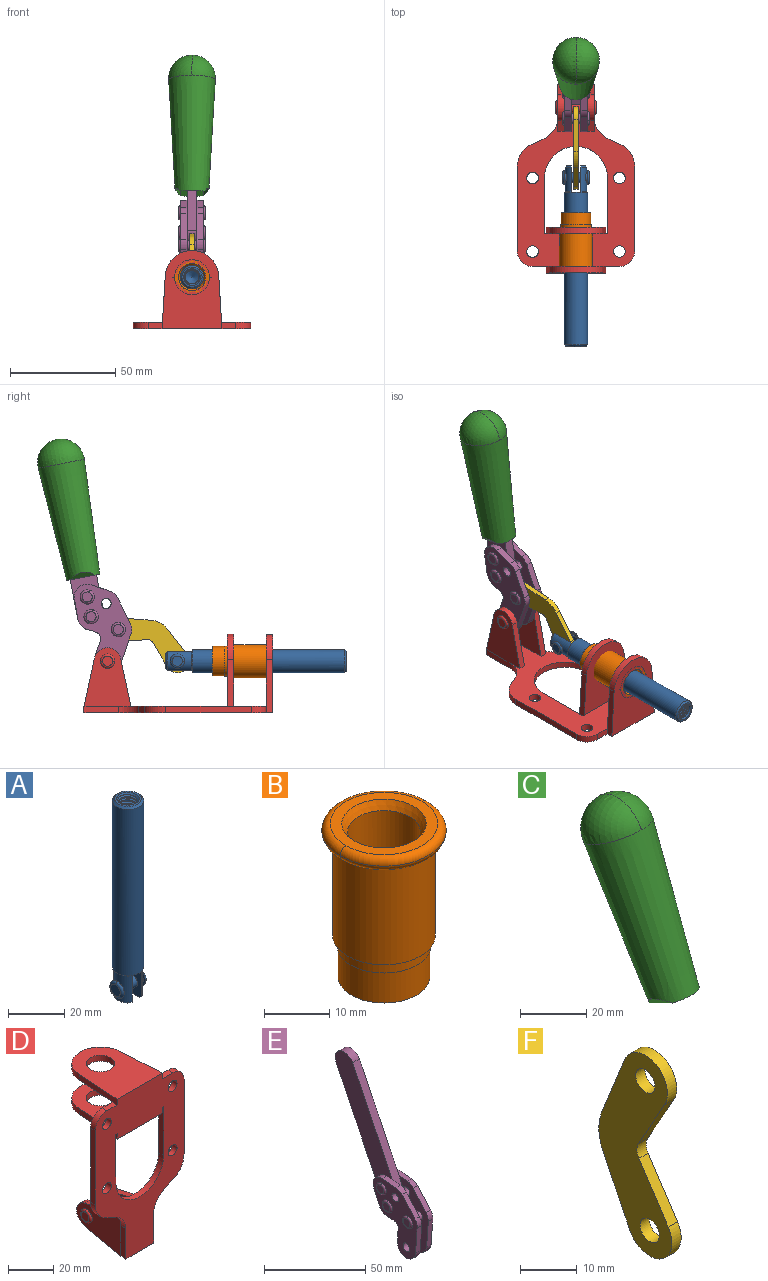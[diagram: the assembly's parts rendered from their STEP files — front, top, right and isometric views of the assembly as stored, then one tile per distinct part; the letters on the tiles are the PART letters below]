
ASSEMBLY  parts=6 mates=6
PART A: 48 faces, bbox 12.6x11.1x86.1 mm
  f0: torus R=2.41mm, axis (-1,0,0), area 15mm2, adj f30,f32,f34
  f1: torus R=2.41mm, axis (-1,0,0), area 15mm2, adj f29,f31,f33
  f2: cylinder r=5.54mm len=72.39mm, axis (0,0,1), area 2518.5mm2, adj f3,f4,f42,f43
  f3: cone r=5.54mm half-angle=45deg, axis (0,0,1), area 7.6mm2, adj f2,f5,f41
  f4: cone r=5.54mm half-angle=45deg, axis (0,0,-1), area 34.9mm2, adj f2,f39
  f5: cylinder r=5.08mm len=11.48mm, axis (0,0,1), area 108.3mm2, adj f3,f7,f8,f41
  f6: cylinder r=2.41mm len=4.83mm, axis (-1,0,0), area 71.2mm2, adj f40,f41
  f7: cylinder r=2.41mm len=4.83mm, axis (-1,0,0), area 7.6mm2, adj f5,f34
  f8: cone r=5.08mm half-angle=45deg, axis (0,0,1), area 10.6mm2, adj f5,f37,f41
  f9: cone r=3.98mm half-angle=45deg, axis (0,0,1), area 17.6mm2, adj f27,f39,f45,f46,f47
  f10: cylinder r=2.41mm len=4.83mm, axis (-1,0,0), area 7.6mm2, adj f33,f38
  f11: cylinder r=3.2mm len=6.4mm, axis (0,0,1), area 78.4mm2, adj f12,f28,f44,f45,f47
  f12: cylinder r=3.2mm len=6.4mm, axis (0,0,1), area 10.5mm2, adj f11,f13,f45,f47
  f13: cylinder r=3.2mm len=6.4mm, axis (0,0,1), area 10.5mm2, adj f12,f14,f45,f47
  f14: cylinder r=3.2mm len=6.4mm, axis (0,0,1), area 10.5mm2, adj f13,f15,f45,f47
  f15: cylinder r=3.2mm len=6.4mm, axis (0,0,1), area 10.5mm2, adj f14,f16,f45,f47
  f16: cylinder r=3.2mm len=6.4mm, axis (0,0,1), area 10.5mm2, adj f15,f17,f45,f47
  f17: cylinder r=3.2mm len=6.4mm, axis (0,0,1), area 10.5mm2, adj f16,f18,f45,f47
  f18: cylinder r=3.2mm len=6.4mm, axis (0,0,1), area 10.5mm2, adj f17,f19,f45,f47
  f19: cylinder r=3.2mm len=6.4mm, axis (0,0,1), area 10.5mm2, adj f18,f20,f45,f47
  f20: cylinder r=3.2mm len=6.4mm, axis (0,0,1), area 10.5mm2, adj f19,f21,f45,f47
  f21: cylinder r=3.2mm len=6.4mm, axis (0,0,1), area 10.5mm2, adj f20,f22,f45,f47
  f22: cylinder r=3.2mm len=6.4mm, axis (0,0,1), area 10.5mm2, adj f21,f23,f45,f47
  f23: cylinder r=3.2mm len=6.4mm, axis (0,0,1), area 10.5mm2, adj f22,f24,f45,f47
  f24: cylinder r=3.2mm len=6.4mm, axis (0,0,1), area 10.5mm2, adj f23,f25,f45,f47
  f25: cylinder r=3.2mm len=6.4mm, axis (0,0,1), area 10.5mm2, adj f24,f26,f45,f47
  f26: cylinder r=3.2mm len=6.4mm, axis (0,0,1), area 10.5mm2, adj f25,f27,f45,f47
  f27: cylinder r=3.2mm len=6.4mm, axis (0,0,1), area 7.4mm2, adj f9,f26,f45,f47
  f28: cone r=3.2mm half-angle=60deg, axis (0,0,1), area 37.2mm2, adj f11
  f29: plane 4.83x4.83mm, normal (-1,0,0), area 18.3mm2, adj f1,f31
  f30: plane 4.83x4.83mm, normal (1,0,0), area 18.3mm2, adj f0,f32
  f31: torus R=2.41mm, axis (-1,0,0), area 15mm2, adj f1,f29,f33
  f32: torus R=2.41mm, axis (-1,0,0), area 15mm2, adj f0,f30,f34
  f33: plane 6.83x6.83mm, normal (1,0,0), area 18.3mm2, adj f1,f10,f31
  f34: plane 6.83x6.83mm, normal (-1,0,0), area 18.3mm2, adj f0,f7,f32
  f35: cone r=5.08mm half-angle=45deg, axis (0,0,1), area 10.6mm2, adj f36,f38,f40
  f36: plane 7.25x1.97mm, normal (0,0,-1), area 10mm2, adj f35,f40
  f37: plane 7.25x1.97mm, normal (0,0,-1), area 10mm2, adj f8,f41
  f38: cylinder r=5.08mm len=11.48mm, axis (0,0,1), area 108.3mm2, adj f10,f35,f40,f42
  f39: plane 9.55x9.55mm, normal (0,0,1), area 22mm2, adj f4,f9
  f40: plane 12.76x10.09mm, normal (1,0,0), area 95.7mm2, adj f6,f35,f36,f38,f42,f43
  f41: plane 12.76x10.09mm, normal (-1,0,0), area 95.7mm2, adj f3,f5,f6,f8,f37,f43
  f42: cone r=5.54mm half-angle=45deg, axis (0,0,1), area 7.6mm2, adj f2,f38,f40
  f43: plane 11.07x4.7mm, normal (0,0,-1), area 50.4mm2, adj f2,f40,f41
  f44: plane 0.89x0.62mm, normal (-1,0,0), area 0.3mm2, adj f11,f45,f46,f47
  f45: bspline ~24.8x7.63mm, area 266.6mm2, adj f9,f11,f12,f13,f14,f15,f16,f17
  f46: bspline ~24.87x7.63mm, area 73.6mm2, adj f9,f44,f45,f47
  f47: bspline ~24.98x7.63mm, area 272.5mm2, adj f9,f11,f12,f13,f14,f15,f16,f17
PART B: 15 faces, bbox 20.6x20.6x28.7 mm
  f0: torus R=8.26mm, axis (0,0,1), area 56.8mm2, adj f1,f10,f12
  f1: torus R=8.26mm, axis (0,0,1), area 56.8mm2, adj f0,f6,f13
  f2: cylinder r=5.59mm len=25.91mm, axis (0,0,1), area 909.6mm2, adj f3,f4
  f3: cone r=6.86mm half-angle=45deg, axis (0,0,-1), area 70.2mm2, adj f2,f14
  f4: cone r=6.47mm half-angle=30deg, axis (0,0,1), area 66.7mm2, adj f2,f13
  f5: cylinder r=7.04mm len=14.07mm, axis (0,0,1), area 252.6mm2, adj f11,f14
  f6: torus R=8.26mm, axis (0,0,1), area 56.8mm2, adj f1,f12,f13
  f7: cylinder r=7.16mm len=14.33mm, axis (0,0,1), area 91.5mm2, adj f9,f11
  f8: cylinder r=7.86mm len=18.42mm, axis (0,0,1), area 909.6mm2, adj f9,f10
  f9: plane 15.72x15.72mm, normal (0,0,-1), area 33mm2, adj f7,f8
  f10: plane 16.51x16.51mm, normal (0,0,-1), area 19.9mm2, adj f0,f8,f12
  f11: plane 14.33x14.33mm, normal (0,0,-1), area 5.7mm2, adj f5,f7
  f12: torus R=8.26mm, axis (0,0,1), area 56.8mm2, adj f0,f6,f10
  f13: plane 16.51x16.51mm, normal (0,0,1), area 82.7mm2, adj f1,f4,f6
  f14: plane 14.07x14.07mm, normal (0,0,-1), area 7.8mm2, adj f3,f5
PART C: 11 faces, bbox 22.3x42.6x64.5 mm
  f0: sphere r=11.13mm, area 411.4mm2, adj f1,f8
  f1: cone r=11.11mm half-angle=3.3deg, axis (0,0.44,0.9), area 3251.8mm2, adj f0,f7,f8,f9,f10
  f2: cylinder r=6.16mm len=11.7mm, axis (1,0,0), area 89.5mm2, adj f3,f4,f5,f6
  f3: plane 60.23x36.75mm, normal (-1,0,0), area 763.6mm2, adj f2,f4,f6,f10
  f4: plane 51.37x25.05mm, normal (0,0.9,-0.44), area 264.2mm2, adj f2,f3,f5,f10
  f5: plane 60.23x36.75mm, normal (1,0,0), area 763.6mm2, adj f2,f4,f6,f10
  f6: plane 51.37x25.05mm, normal (0,-0.9,0.44), area 264.2mm2, adj f2,f3,f5,f10
  f7: plane 9.95x5.95mm, normal (0.71,-0.31,-0.64), area 25.8mm2, adj f1,f10
  f8: sphere r=11.13mm, area 411.4mm2, adj f0,f1
  f9: plane 9.95x5.95mm, normal (-0.71,-0.31,-0.64), area 25.8mm2, adj f1,f10
  f10: plane 14.27x11.38mm, normal (0,-0.44,-0.9), area 106.7mm2, adj f1,f3,f4,f5,f6,f7,f9
PART D: 55 faces, bbox 55.7x37.4x89.8 mm
  f0: torus R=2.41mm, axis (-1,0,0), area 15mm2, adj f11,f15,f25
  f1: torus R=2.41mm, axis (-1,0,0), area 15mm2, adj f10,f12,f22
  f2: cylinder r=2.78mm len=5.56mm, axis (0,-1,0), area 54.2mm2, adj f30,f54
  f3: cylinder r=14.99mm len=29.97mm, axis (0,-1,0), area 145.9mm2, adj f30,f49,f53,f54
  f4: cylinder r=2.78mm len=5.56mm, axis (0,-1,0), area 54.2mm2, adj f30,f54
  f5: cylinder r=2.78mm len=5.56mm, axis (0,-1,0), area 54.2mm2, adj f30,f54
  f6: cylinder r=2.78mm len=5.56mm, axis (0,-1,0), area 54.2mm2, adj f30,f54
  f7: cylinder r=6.35mm len=12.7mm, axis (0,0,1), area 123.6mm2, adj f27,f51
  f8: cylinder r=6.35mm len=12.7mm, axis (0,0,-1), area 124.7mm2, adj f21,f35
  f9: cylinder r=2.41mm len=11.18mm, axis (-1,0,0), area 169.4mm2, adj f16,f19
  f10: plane 4.83x4.83mm, normal (1,0,0), area 18.3mm2, adj f1,f12
  f11: plane 4.83x4.83mm, normal (-1,0,0), area 18.3mm2, adj f0,f15
  f12: torus R=2.41mm, axis (-1,0,0), area 15mm2, adj f1,f10,f22
  f13: cylinder r=6.35mm len=12.41mm, axis (1,0,0), area 53.4mm2, adj f18,f19,f22,f23
  f14: cylinder r=6.35mm len=12.41mm, axis (-1,0,0), area 53.4mm2, adj f16,f17,f24,f25
  f15: torus R=2.41mm, axis (-1,0,0), area 15mm2, adj f0,f11,f25
  f16: plane 27.86x22.35mm, normal (1,0,0), area 425.4mm2, adj f9,f14,f17,f24,f30
  f17: plane 22.86x4.97mm, normal (0,0.21,0.98), area 72.5mm2, adj f14,f16,f25,f30
  f18: plane 22.86x4.97mm, normal (0,0.21,0.98), area 72.5mm2, adj f13,f19,f22,f30
  f19: plane 27.86x22.35mm, normal (-1,0,0), area 425.4mm2, adj f9,f13,f18,f23,f30
  f20: cylinder r=12.7mm len=25.35mm, axis (0,0,-1), area 119.8mm2, adj f21,f34,f35,f36
  f21: plane 34.21x28.07mm, normal (0,0,-1), area 702.4mm2, adj f8,f20,f30,f34,f36
  f22: plane 27.96x22.45mm, normal (1,0,0), area 407.2mm2, adj f1,f12,f13,f18,f23,f30,f42,f43
  f23: plane 22.86x4.97mm, normal (0,0.21,-0.98), area 72.5mm2, adj f13,f19,f22,f44
  f24: plane 22.86x4.97mm, normal (0,0.21,-0.98), area 72.5mm2, adj f14,f16,f25,f44
  f25: plane 27.86x22.35mm, normal (-1,0,0), area 407.1mm2, adj f0,f14,f15,f17,f24,f30,f45,f46
  f26: plane 3.1x0.95mm, normal (0,0,-1), area 2.7mm2, adj f30,f49,f50,f54
  f27: plane 34.21x28.07mm, normal (0,0,1), area 702.4mm2, adj f7,f28,f30,f50,f52
  f28: cylinder r=12.7mm len=25.35mm, axis (0,0,1), area 118.8mm2, adj f27,f50,f51,f52
  f29: plane 3.1x0.95mm, normal (0,0,-1), area 2.7mm2, adj f30,f52,f53,f54
  f30: plane 86.54x55.63mm, normal (0,1,0), area 2362.9mm2, adj f2,f3,f4,f5,f6,f16,f17,f18
  f31: plane 40.56x3.1mm, normal (-1,0,0), area 125.7mm2, adj f30,f32,f48,f54
  f32: cylinder r=7.11mm len=7.11mm, axis (0,-1,0), area 34.6mm2, adj f30,f31,f33,f54
  f33: plane 6.67x3.1mm, normal (0,0,1), area 20.4mm2, adj f30,f32,f34,f54
  f34: plane 25.39x3.13mm, normal (-1,0.06,0), area 79.5mm2, adj f20,f21,f33,f35,f54
  f35: plane 37.31x28.45mm, normal (0,0,1), area 789.9mm2, adj f8,f20,f34,f36,f54
  f36: plane 25.39x3.13mm, normal (1,0.06,0), area 79.5mm2, adj f20,f21,f35,f37,f54
  f37: plane 6.67x3.1mm, normal (0,0,1), area 20.4mm2, adj f30,f36,f38,f54
  f38: cylinder r=7.11mm len=7.11mm, axis (0,-1,0), area 34.6mm2, adj f30,f37,f39,f54
  f39: plane 40.56x3.1mm, normal (1,0,0), area 125.7mm2, adj f30,f38,f40,f54
  f40: cylinder r=11.18mm len=10.16mm, axis (0,-1,0), area 39.5mm2, adj f30,f39,f41,f54
  f41: plane 6.09x3.1mm, normal (0.42,0,-0.91), area 20.8mm2, adj f30,f40,f42,f54
  f42: cylinder r=11.18mm len=9.41mm, axis (0,-1,0), area 37.2mm2, adj f22,f30,f41,f43,f54
  f43: plane 16.5x3.1mm, normal (1,0,0), area 51.1mm2, adj f22,f42,f44,f54
  f44: plane 17.37x3.1mm, normal (0,0,-1), area 53.8mm2, adj f23,f24,f30,f43,f45,f54
  f45: plane 16.5x3.1mm, normal (-1,0,0), area 51.1mm2, adj f25,f44,f46,f54
  f46: cylinder r=11.18mm len=9.41mm, axis (0,-1,0), area 37.2mm2, adj f25,f30,f45,f47,f54
  f47: plane 6.09x3.1mm, normal (-0.42,0,-0.91), area 20.8mm2, adj f30,f46,f48,f54
  f48: cylinder r=11.18mm len=10.16mm, axis (0,-1,0), area 39.5mm2, adj f30,f31,f47,f54
  f49: plane 26.54x3.1mm, normal (-1,0,0), area 82.3mm2, adj f3,f26,f30,f54
  f50: plane 25.39x3.1mm, normal (1,0.06,0), area 78.8mm2, adj f26,f27,f28,f51,f54
  f51: plane 37.31x28.45mm, normal (0,0,-1), area 789.9mm2, adj f7,f28,f50,f52,f54
  f52: plane 25.39x3.1mm, normal (-1,0.06,0), area 78.8mm2, adj f27,f28,f29,f51,f54
  f53: plane 26.54x3.1mm, normal (1,0,0), area 82.3mm2, adj f3,f29,f30,f54
  f54: plane 89.66x55.63mm, normal (0,-1,0), area 2678.5mm2, adj f2,f3,f4,f5,f6,f26,f29,f31
PART E: 59 faces, bbox 12.9x60.2x99.6 mm
  f0: torus R=2.39mm, axis (-1,0,0), area 14.9mm2, adj f20,f43,f51
  f1: torus R=2.39mm, axis (-1,0,0), area 14.9mm2, adj f19,f42,f51
  f2: torus R=2.39mm, axis (-1,0,0), area 14.9mm2, adj f18,f35,f51
  f3: torus R=2.39mm, axis (-1,0,0), area 14.9mm2, adj f14,f17,f23
  f4: torus R=2.39mm, axis (-1,0,0), area 14.9mm2, adj f13,f16,f23
  f5: torus R=2.39mm, axis (-1,0,0), area 14.9mm2, adj f12,f15,f23
  f6: cylinder r=2.39mm len=4.78mm, axis (1,0,0), area 46.5mm2, adj f48,f50,f51
  f7: cylinder r=2.39mm len=4.78mm, axis (1,0,0), area 46.5mm2, adj f50,f51
  f8: cylinder r=6.35mm len=12.68mm, axis (1,0,0), area 61.8mm2, adj f38,f39,f50,f51
  f9: cylinder r=2.39mm len=4.78mm, axis (-1,0,0), area 70.5mm2, adj f46,f50
  f10: cylinder r=2.39mm len=4.78mm, axis (-1,0,0), area 46.5mm2, adj f23,f45,f46
  f11: cylinder r=2.39mm len=4.78mm, axis (-1,0,0), area 46.5mm2, adj f23,f46
  f12: plane 4.78x4.78mm, normal (1,0,0), area 17.9mm2, adj f5,f15
  f13: plane 4.78x4.78mm, normal (1,0,0), area 17.9mm2, adj f4,f16
  f14: plane 4.78x4.78mm, normal (1,0,0), area 17.9mm2, adj f3,f17
  f15: torus R=2.39mm, axis (-1,0,0), area 14.9mm2, adj f5,f12,f23
  f16: torus R=2.39mm, axis (-1,0,0), area 14.9mm2, adj f4,f13,f23
  f17: torus R=2.39mm, axis (-1,0,0), area 14.9mm2, adj f3,f14,f23
  f18: plane 4.78x4.78mm, normal (-1,0,0), area 17.9mm2, adj f2,f35
  f19: plane 4.78x4.78mm, normal (-1,0,0), area 17.9mm2, adj f1,f42
  f20: plane 4.78x4.78mm, normal (-1,0,0), area 17.9mm2, adj f0,f43
  f21: plane 2.26x0.2mm, normal (1,0,0), area 0.2mm2, adj f31,f44
  f22: plane 2.26x0.2mm, normal (-1,0,0), area 0.2mm2, adj f41,f44
  f23: plane 39.37x30.77mm, normal (1,0,0), area 565.5mm2, adj f3,f4,f5,f10,f11,f15,f16,f17
  f24: cylinder r=6.1mm len=4.15mm, axis (-1,0,0), area 14.7mm2, adj f23,f25,f32,f46
  f25: plane 10.25x9.01mm, normal (0,-0.75,0.66), area 42.3mm2, adj f23,f24,f26,f46
  f26: cylinder r=6.35mm len=4.64mm, axis (-1,0,0), area 15.6mm2, adj f23,f25,f27,f46
  f27: plane 15.84x3.1mm, normal (0,-1,-0.07), area 49.2mm2, adj f23,f26,f28,f46
  f28: cylinder r=6.35mm len=12.68mm, axis (-1,0,0), area 61.8mm2, adj f23,f27,f29,f46
  f29: plane 8.11x3.1mm, normal (0,1,0.07), area 25.2mm2, adj f23,f28,f30,f46
  f30: cylinder r=3.05mm len=3.25mm, axis (-1,0,0), area 14.8mm2, adj f23,f29,f31,f46
  f31: plane 5.99x3.1mm, normal (0,0.07,-1), area 18.6mm2, adj f21,f23,f30,f44,f46
  f32: plane 9.5x3.1mm, normal (0,-0.07,1), area 29.5mm2, adj f23,f24,f33,f46,f47
  f33: cylinder r=6.1mm len=8.63mm, axis (-1,0,0), area 39.1mm2, adj f23,f32,f34,f47
  f34: plane 8.65x3.96mm, normal (0,0.91,-0.42), area 29.5mm2, adj f23,f33,f44,f47
  f35: torus R=2.39mm, axis (-1,0,0), area 14.9mm2, adj f2,f18,f51
  f36: plane 10.25x9.01mm, normal (0,-0.75,0.66), area 42.3mm2, adj f37,f49,f50,f51
  f37: cylinder r=6.35mm len=4.64mm, axis (1,0,0), area 15.6mm2, adj f36,f38,f50,f51
  f38: plane 15.84x3.1mm, normal (0,-1,-0.07), area 49.2mm2, adj f8,f37,f50,f51
  f39: plane 8.11x3.1mm, normal (0,1,0.07), area 25.2mm2, adj f8,f40,f50,f51
  f40: cylinder r=3.05mm len=3.25mm, axis (1,0,0), area 14.8mm2, adj f39,f41,f50,f51
  f41: plane 5.99x3.1mm, normal (0,0.07,-1), area 18.6mm2, adj f22,f40,f44,f50,f51
  f42: torus R=2.39mm, axis (-1,0,0), area 14.9mm2, adj f1,f19,f51
  f43: torus R=2.39mm, axis (-1,0,0), area 14.9mm2, adj f0,f20,f51
  f44: cylinder r=6.35mm len=12.12mm, axis (-1,0,0), area 128.9mm2, adj f21,f22,f23,f31,f34,f41,f46,f47
  f45: plane 2.65x1.35mm, normal (1,0,0), area 1mm2, adj f10,f55
  f46: plane 39.08x20.42mm, normal (-1,0,0), area 412.5mm2, adj f9,f10,f11,f24,f25,f26,f27,f28
  f47: plane 77.62x39.82mm, normal (1,0,0), area 850mm2, adj f32,f33,f34,f44,f53,f54,f55
  f48: plane 2.65x1.35mm, normal (-1,0,0), area 1mm2, adj f6,f55
  f49: cylinder r=6.1mm len=4.15mm, axis (1,0,0), area 14.7mm2, adj f36,f50,f51,f56
  f50: plane 39.08x20.42mm, normal (1,0,0), area 412.5mm2, adj f6,f7,f8,f9,f36,f37,f38,f39
  f51: plane 39.37x30.77mm, normal (-1,0,0), area 565.5mm2, adj f0,f1,f2,f6,f7,f8,f35,f36
  f52: plane 8.65x3.96mm, normal (0,0.91,-0.42), area 29.5mm2, adj f44,f51,f57,f58
  f53: plane 68.49x33.4mm, normal (0,0.9,-0.44), area 358.1mm2, adj f44,f47,f54,f58
  f54: cylinder r=6.35mm len=12.06mm, axis (1,0,0), area 93.7mm2, adj f47,f53,f55,f58
  f55: plane 68.49x33.4mm, normal (0,-0.9,0.44), area 358.1mm2, adj f44,f45,f46,f47,f48,f50,f54,f58
  f56: plane 9.5x3.1mm, normal (0,-0.07,1), area 29.5mm2, adj f49,f50,f51,f57,f58
  f57: cylinder r=6.1mm len=8.63mm, axis (1,0,0), area 39.1mm2, adj f51,f52,f56,f58
  f58: plane 77.62x39.82mm, normal (-1,0,0), area 850mm2, adj f44,f52,f53,f54,f55,f56,f57
PART F: 12 faces, bbox 2.3x18.2x42.8 mm
  f0: cylinder r=2.4mm len=4.8mm, axis (1,0,0), area 34.9mm2, adj f4,f11
  f1: cylinder r=10.41mm len=8.47mm, axis (1,0,0), area 20.2mm2, adj f4,f9,f10,f11
  f2: cylinder r=3.05mm len=3.16mm, axis (1,0,0), area 7.7mm2, adj f4,f6,f7,f11
  f3: cylinder r=2.4mm len=4.8mm, axis (1,0,0), area 34.9mm2, adj f4,f11
  f4: plane 42.81x18.23mm, normal (-1,0,0), area 414.1mm2, adj f0,f1,f2,f3,f5,f6,f7,f8
  f5: cylinder r=5.54mm len=10.67mm, axis (1,0,0), area 41.8mm2, adj f4,f6,f10,f11
  f6: plane 11.66x6.53mm, normal (0,-0.87,-0.49), area 30.9mm2, adj f2,f4,f5,f11
  f7: plane 11.17x7.33mm, normal (0,-0.84,0.55), area 30.9mm2, adj f2,f4,f8,f11
  f8: cylinder r=5.54mm len=10.51mm, axis (1,0,0), area 41.8mm2, adj f4,f7,f9,f11
  f9: plane 13.67x6.67mm, normal (0,0.9,-0.44), area 35.1mm2, adj f1,f4,f8,f11
  f10: plane 14.1x5.7mm, normal (0,0.93,0.37), area 35.1mm2, adj f1,f4,f5,f11
  f11: plane 42.81x18.23mm, normal (1,0,0), area 414.1mm2, adj f0,f1,f2,f3,f5,f6,f7,f8
PLACE A rot(axis=(1,0,0),90deg) t=(0,23.56,0)mm
PLACE B rot(axis=(1,0,0),90deg) t=(0,11.68,0)mm
PLACE C rot(axis=(1,0,0),15deg) t=(0,9.15,49.24)mm
PLACE D rot(axis=(1,0,0),90deg) t=(0,9.14,0)mm fixed
PLACE E rot(axis=(1,0,0),15deg) t=(0,9.15,49.24)mm
PLACE F rot(axis=(1,0,0),120.2deg) t=(0,33.84,11.13)mm
MATE revolute E.f7 <-> D.f0  axis (-1,0,0) through (0,41.23,24.61)mm
MATE fastened B.f12 <-> D.f7  axis (0,-1,0) through (0,-37.25,24.61)mm
MATE slider A.f2 <-> D.f7  axis (0,-1,0) through (0,-35.22,24.61)mm
MATE revolute F.f5 <-> A.f6  axis (1,0,0) through (0,8.09,24.61)mm
MATE revolute F.f3 <-> E.f4  axis (1,0,0) through (0,36.06,39.62)mm
MATE fastened C.f2 <-> E.f54  axis (1,0,0) through (0,63.6,120.54)mm
